FCSTD DOCUMENT  (FreeCAD 0.21R33694 (Git))
Label: OJT1_T18R01.viga
License: All rights reserved
LicenseURL: http://en.wikipedia.org/wiki/All_rights_reserved
objects: Sketcher::SketchObject×1, PartDesign::Body×1
note: 2 computed .brp shape members not serialized (recipe doc carries the construction recipe); baked Part::Feature solids carry a one-line shape summary decoded from their .brp

FEATURE [Sketcher::SketchObject] Sketch
  FullyConstrained = false
  MapMode = 5
  Support = -> [XY_Plane]
  sketch-geometry (12):
    g0: LineSegment StartX=0 StartY=0 StartZ=0 EndX=0 EndY=12 EndZ=0
    g1: LineSegment StartX=0 StartY=12 StartZ=0 EndX=40 EndY=12 EndZ=0
    g2: LineSegment StartX=40 StartY=12 StartZ=0 EndX=40 EndY=62.9998 EndZ=0
    g3: LineSegment StartX=40 StartY=62.9998 StartZ=0 EndX=0.172358 EndY=62.9998 EndZ=0
    g4: LineSegment StartX=0.172358 StartY=62.9998 StartZ=0 EndX=0.172358 EndY=74.9998 EndZ=0
    g5: LineSegment StartX=0.172358 StartY=74.9998 StartZ=0 EndX=90.1724 EndY=74.9998 EndZ=0
    g6: LineSegment StartX=90.1724 StartY=74.9998 StartZ=0 EndX=90.1724 EndY=62.9998 EndZ=0
    g7: LineSegment StartX=90.1724 StartY=62.9998 StartZ=0 EndX=50 EndY=62.9998 EndZ=0
    g8: LineSegment StartX=50 StartY=62.9998 StartZ=0 EndX=50 EndY=12 EndZ=0
    g9: LineSegment StartX=50 StartY=12 StartZ=0 EndX=90 EndY=12 EndZ=0
    g10: LineSegment StartX=90 StartY=12 StartZ=0 EndX=90 EndY=0 EndZ=0
    g11: LineSegment StartX=90 StartY=0 StartZ=0 EndX=0 EndY=0 EndZ=0
  constraints (34):
    c: Coincident(g-1,g0)
    c: Coincident(g0,g1)
    c: Coincident(g1,g2)
    c: Coincident(g2,g3)
    c: Coincident(g3,g4)
    c: Coincident(g4,g5)
    c: Horizontal(g5)
    c: Coincident(g5,g6)
    c: Coincident(g6,g7)
    c: Coincident(g7,g8)
    c: Coincident(g8,g9)
    c: Coincident(g9,g10)
    c: PointOnObject(g10,g-1)
    c: Vertical(g10)
    c: Coincident(g10,g11)
    c: Coincident(g11,g0)
    c: DistanceX(g11,g11) = 90
    c: DistanceY(g10,g10) = 12
    c: Vertical(g0)
    c: Horizontal(g3)
    c: Vertical(g4)
    c: Horizontal(g7)
    c: Vertical(g6)
    c: Vertical(g8)
    c: Horizontal(g9)
    c: Horizontal(g1)
    c: Vertical(g2)
    c: Equal(g8,g2)
    c: Equal(g11,g5)
    c: Equal(g0,g10)
    c: Equal(g0,g4)
    c: Equal(g1,g9)
    c: Distance(g2,g7) = 10
    c: Distance(g4,g0) = 75
FEATURE [PartDesign::Body] Body
  Group = -> [Sketch]
  Origin = -> Origin
